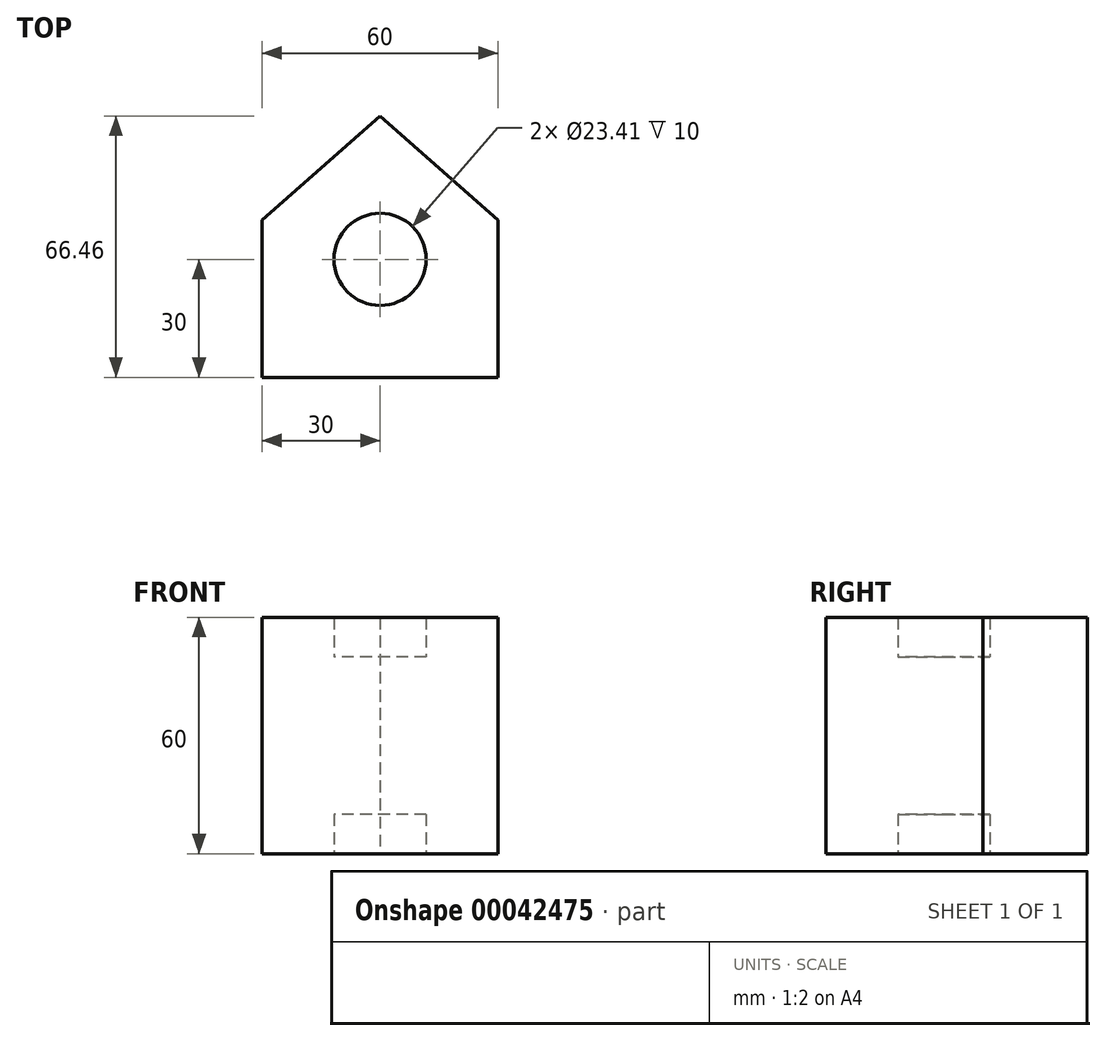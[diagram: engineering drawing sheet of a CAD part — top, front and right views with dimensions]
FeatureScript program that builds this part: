
annotation { "Feature Type Name" : "Feature", "Feature Type Description" : "" }
export const myFeature = defineFeature(function(context is Context, id is Id, definition is map)
    precondition{}
    {
        {
            var Q0;
            Q0=qCreatedBy(makeId("Top.planeOp"),FACE);
            var sketch = newSketch(context, id + "F0", { "sketchPlane" : qUnion([Q0])});
            skLineSegment(sketch, "E0", {"start": v(-60, 0) * mm, "end": v(0, 0) * mm});
            skLineSegment(sketch, "E1", {"start": v(0, 0) * mm, "end": v(0, 40) * mm});
            skLineSegment(sketch, "E2", {"start": v(-60, 40) * mm, "end": v(-60, 0) * mm});
            skLineSegment(sketch, "E3", {"start": v(-60, 40) * mm, "end": v(-30, 66.46) * mm});
            skLineSegment(sketch, "E4", {"start": v(-30, 66.46) * mm, "end": v(0, 40) * mm});
            skCircle(sketch, "E5", {"center": v(-30, 30) * mm, "radius": 11.7 * mm});
            skSolve(sketch);
        }
        {
            var Q0;
            Q0=makeQuery(id+"F0.imprint","IMPRINT",FACE,{"disambiguationData":[TD([[makeQuery(id+"F0.imprint","IMPRINT",EDGE,{"derivedFrom":sQuery(id+"F0.wireOp",EDGE,"E0")}),1.0]])]});
            var Q1;
            Q1=makeQuery(id+"F0.imprint","IMPRINT",FACE,{"disambiguationData":[TD([[makeQuery(id+"F0.imprint","IMPRINT",EDGE,{"derivedFrom":sQuery(id+"F0.wireOp",EDGE,"baa5647d-1bb2-482e-932c-1fec2d820148")}),-1.0]])]});
            extrude(context, id + "F1", {"entities" : qUnion([Q0, Q1]), "depth" : 60 * mm});
        }
        {
            var Q0;
            Q0=makeQuery(id+"F0.imprint","IMPRINT",FACE,{"disambiguationData":[TD([[makeQuery(id+"F0.imprint","IMPRINT",EDGE,{"derivedFrom":sQuery(id+"F0.wireOp",EDGE,"E5")}),1.0]])]});
            extrude(context, id + "F2", {"entities" : qUnion([Q0]), "operationType" : NewBodyOperationType.ADD, "depth" : 50 * mm, "hasSecondDirection" : true, "secondDirectionOppositeDirection" : false, "secondDirectionDepth" : 10 * mm});
        }
    });
